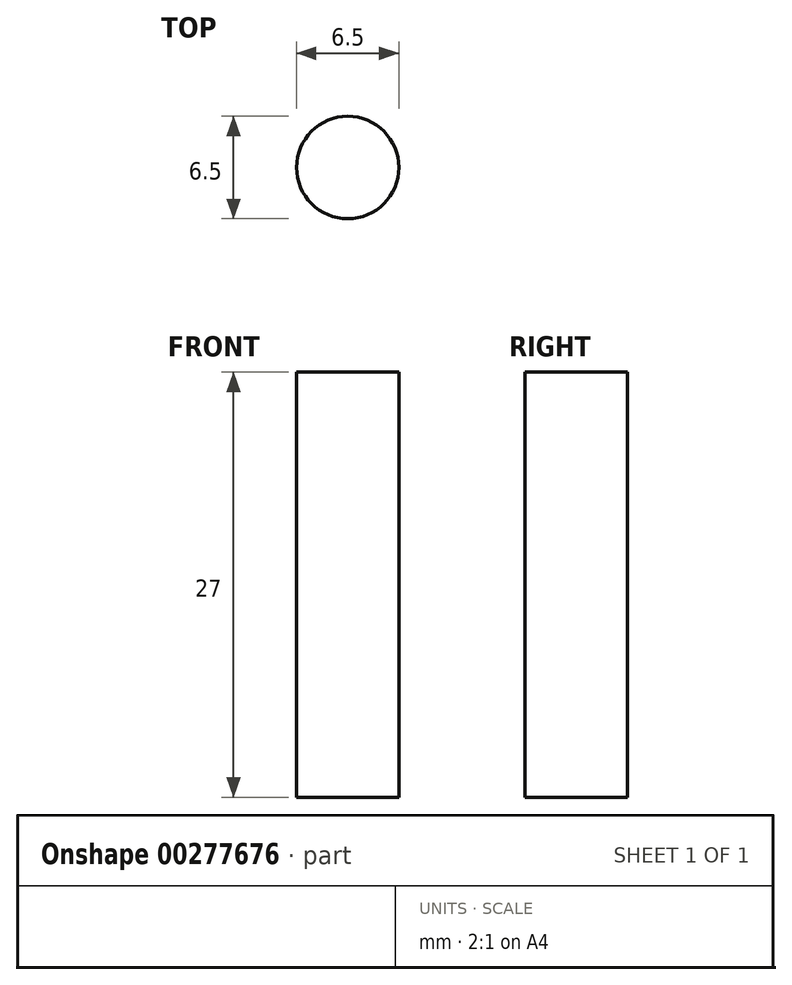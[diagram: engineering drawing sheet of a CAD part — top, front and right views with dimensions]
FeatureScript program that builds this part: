
annotation { "Feature Type Name" : "Feature", "Feature Type Description" : "" }
export const myFeature = defineFeature(function(context is Context, id is Id, definition is map)
    precondition{}
    {
        {
            var Q0;
            Q0=qCreatedBy(makeId("Top.planeOp"),FACE);
            var sketch = newSketch(context, id + "F0", { "sketchPlane" : qUnion([Q0])});
            skCircle(sketch, "E0", {"center": v(0, 0) * mm, "radius": 3.25 * mm});
            skSolve(sketch);
        }
        {
            var Q0;
            Q0 = qSketchRegion(id + "F0", true);
            extrude(context, id + "F1", {"entities" : qUnion([Q0]), "depth" : 27 * mm});
        }
    });
